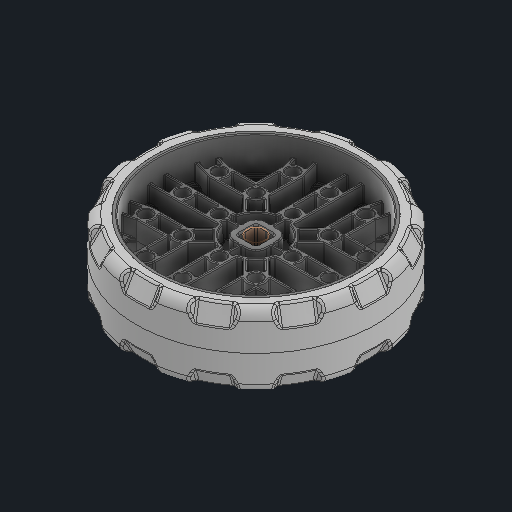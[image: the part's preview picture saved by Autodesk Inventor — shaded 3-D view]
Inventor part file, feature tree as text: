
AUTODESK INVENTOR PART (.ipt)
format: ipt  version: 2024 (Build 280153000, 153)  size: 12,616,704 bytes
history: native  units: in
note: dims shown in document units (in); Inventor stores cm internally (conversion verified against a paired STEP export)
features: other x6, sketch x1
ambient origin geometry x8: Origin, YZ Plane, XZ Plane, XY Plane, X Axis, Y Axis, Z Axis, Center Point
bodies: Solid1 (feature_tree), Solid2 (feature_tree)
feature tree (7):
  other  "3.25 Traction Antistatic.ipt"
  other  "Solid1::3.25 Traction Antistatic.ipt"
  other  "Solid2::3.25 Traction Antistatic.ipt"
  other  "TaggingFeature1"
  sketch  "Sketch1"  dims[d0=0.3937in]
  other  "Srf1"
  other  "Srf1::Derived"
